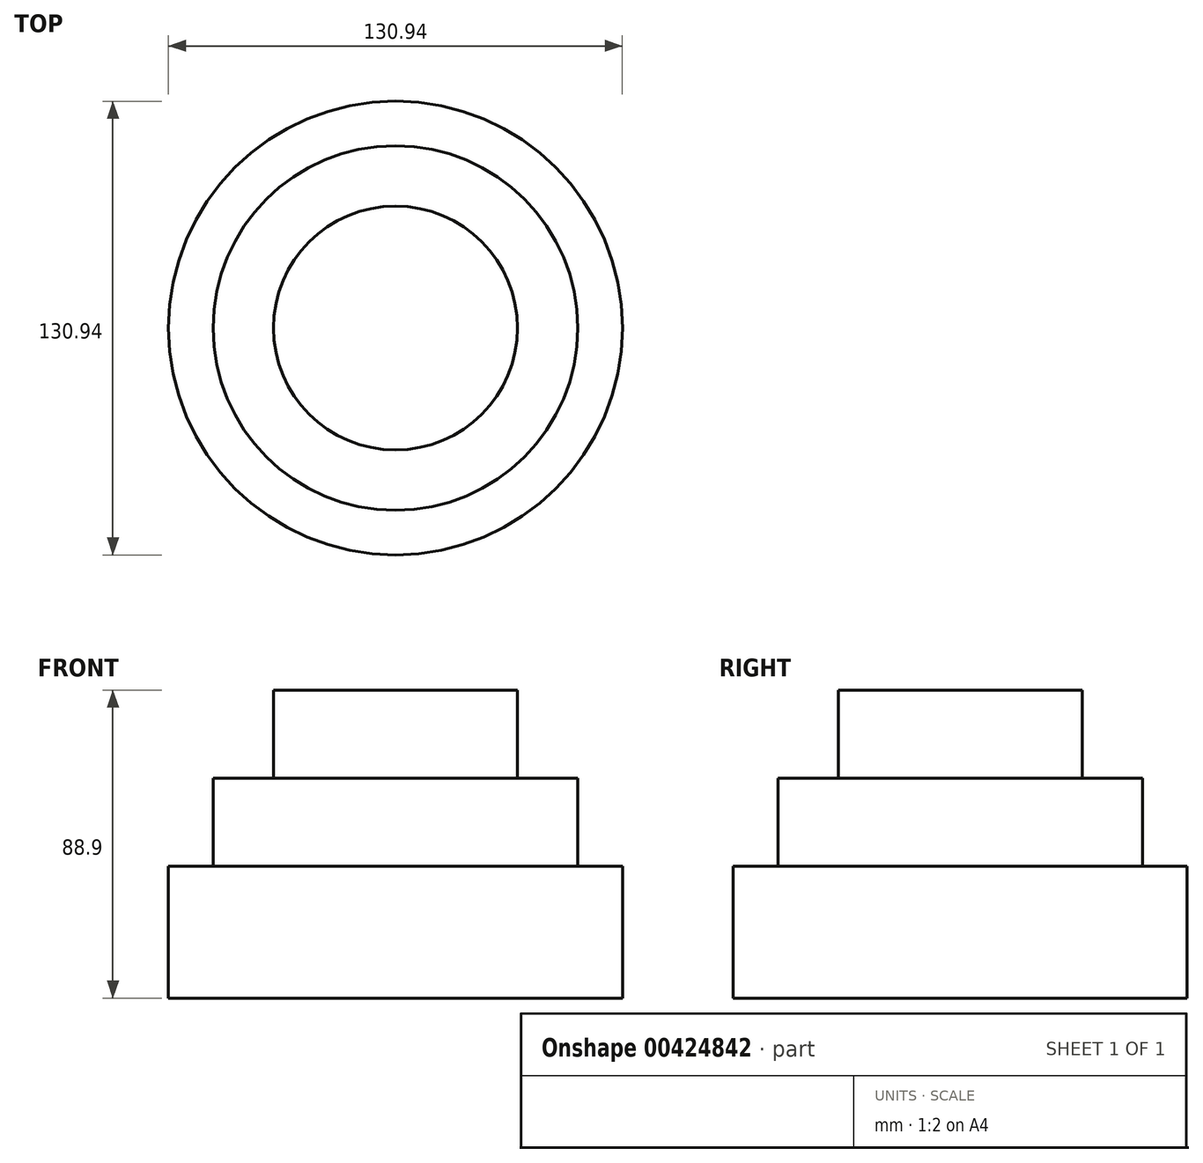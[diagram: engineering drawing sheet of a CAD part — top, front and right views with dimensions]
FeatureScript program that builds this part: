
annotation { "Feature Type Name" : "Feature", "Feature Type Description" : "" }
export const myFeature = defineFeature(function(context is Context, id is Id, definition is map)
    precondition{}
    {
        {
            var Q0;
            Q0=qCreatedBy(makeId("Top.planeOp"),FACE);
            var sketch = newSketch(context, id + "F0", { "sketchPlane" : qUnion([Q0])});
            skCircle(sketch, "E0", {"center": v(0, 0) * mm, "radius": 65.47 * mm});
            skSolve(sketch);
        }
        {
            var Q0;
            Q0=makeQuery(id+"F0.imprint","IMPRINT",FACE,{"disambiguationData":[TD([[makeQuery(id+"F0.imprint","IMPRINT",EDGE,{"derivedFrom":sQuery(id+"F0.wireOp",EDGE,"E0")}),1.0]])]});
            extrude(context, id + "F1", {"entities" : qUnion([Q0]), "depth" : 38.1 * mm});
        }
        {
            var Q0;
            Q0=makeQuery(id+"F1.opExtrude","CAP_FACE",FACE,{"disambiguationData":[OSD([sQuery(id+"F0.wireOp",EDGE,"E0")])],"isStart":false});
            var sketch = newSketch(context, id + "F2", { "sketchPlane" : qUnion([Q0])});
            skCircle(sketch, "E1", {"center": v(0, 0) * mm, "radius": 52.6 * mm});
            skSolve(sketch);
        }
        {
            var Q0;
            Q0=makeQuery(id+"F2.imprint","IMPRINT",FACE,{"disambiguationData":[TD([[makeQuery(id+"F2.imprint","IMPRINT",EDGE,{"derivedFrom":sQuery(id+"F2.wireOp",EDGE,"E1")}),1.0]])]});
            extrude(context, id + "F3", {"entities" : qUnion([Q0]), "operationType" : NewBodyOperationType.ADD, "depth" : 25.4 * mm});
        }
        {
            var Q0;
            Q0=makeQuery(id+"F3.opExtrude","CAP_FACE",FACE,{"disambiguationData":[OSD([sQuery(id+"F2.wireOp",EDGE,"E1")])],"isStart":false});
            var sketch = newSketch(context, id + "F4", { "sketchPlane" : qUnion([Q0])});
            skCircle(sketch, "E2", {"center": v(0, 0) * mm, "radius": 35.18 * mm});
            skSolve(sketch);
        }
        {
            var Q0;
            Q0=makeQuery(id+"F4.imprint","IMPRINT",FACE,{"disambiguationData":[TD([[makeQuery(id+"F4.imprint","IMPRINT",EDGE,{"derivedFrom":sQuery(id+"F4.wireOp",EDGE,"E2")}),1.0]])]});
            extrude(context, id + "F5", {"entities" : qUnion([Q0]), "operationType" : NewBodyOperationType.ADD, "depth" : 25.4 * mm});
        }
        {
            var Q0;
            Q0=makeQuery(id+"F5.opExtrude","CAP_FACE",FACE,{"disambiguationData":[OSD([sQuery(id+"F4.wireOp",EDGE,"E2")])],"isStart":false});
            var sketch = newSketch(context, id + "F6", { "sketchPlane" : qUnion([Q0])});
            skSolve(sketch);
        }
        {
            var Q0;
            Q0=makeQuery(id+"F6.imprint","IMPRINT",FACE,{"disambiguationData":[TD([[makeQuery(id+"F6.imprint","IMPRINT",EDGE,{"derivedFrom":makeQuery(id+"F5.opExtrude","CAP_EDGE",EDGE,{"disambiguationData":[OSD([sQuery(id+"F4.wireOp",EDGE,"E2")])],"isStart":false})}),1.0]])]});
            var sketch = newSketch(context, id + "F7", { "sketchPlane" : qUnion([Q0])});
            skCircle(sketch, "E3", {"center": v(0, 0) * mm, "radius": 4.54 * mm});
            skSolve(sketch);
        }
        {
            var Q0;
            Q0=sQuery(id+"F7.wireOp",EDGE,"E3");
            extrude(context, id + "F8", {"bodyType" : ToolBodyType.SURFACE, "surfaceEntities" : qUnion([Q0]), "depth" : 43.18 * mm});
        }
    });
